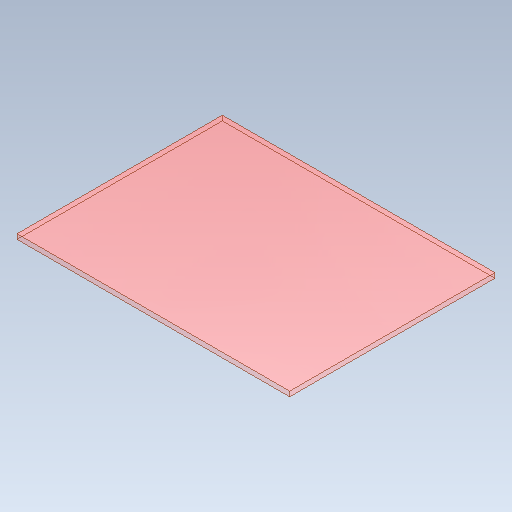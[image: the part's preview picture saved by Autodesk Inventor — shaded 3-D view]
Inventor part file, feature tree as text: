
AUTODESK INVENTOR PART (.ipt)
format: ipt  version: 2021 (Build 250183000, 183)  size: 104,960 bytes
history: native  units: mm
features: extrude x1, sketch x1
ambient origin geometry x8: Origin, YZ Plane, XZ Plane, XY Plane, X Axis, Y Axis, Z Axis, Center Point
bodies: Solid1 (feature_tree)
feature tree (2):
  extrude  "Extrusion1"  Depth=12.5mm
  sketch  "Sketch1"  dims[d0=16.6mm d1=12.5mm d2=0.3mm d3=0.0mm]
